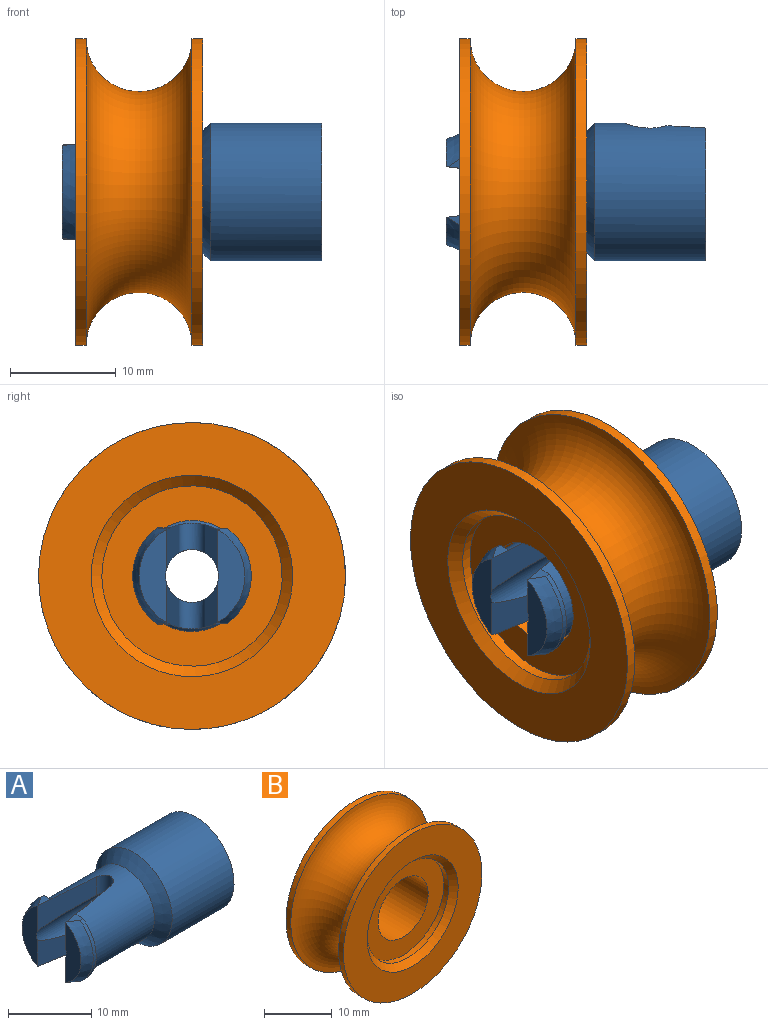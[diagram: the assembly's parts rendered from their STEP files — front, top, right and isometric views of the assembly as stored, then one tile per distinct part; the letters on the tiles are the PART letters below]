
ASSEMBLY  parts=2 mates=1
PART A: 35 faces, bbox 24.6x13.1x13.1 mm
  f0: cylinder r=5mm len=10.5mm, axis (-1,0,0), area 277.7mm2, adj f1,f2,f3,f12,f17,f21,f22,f23
  f1: plane 8.91x4.14mm, normal (-0.13,-0.99,0), area 27.1mm2, adj f0,f3,f5,f7,f15,f24,f32,f33
  f2: plane 8.91x4.14mm, normal (-0.13,0.99,0), area 27mm2, adj f0,f6,f7,f14,f24,f29,f30,f31
  f3: plane 9.12x3.46mm, normal (1,0,0), area 6.6mm2, adj f0,f1,f4,f23,f25,f34
  f4: cylinder r=5.6mm len=9.12mm, axis (-1,0,0), area 5.3mm2, adj f3,f5,f25,f34
  f5: cone r=5.6mm half-angle=21.8deg, axis (1,0,0), area 17.4mm2, adj f1,f4,f15,f23,f25,f34
  f6: plane 8.77x2.6mm, normal (-1,0,0), area 16.1mm2, adj f2,f7,f14,f22
  f7: cylinder r=2.5mm len=14.5mm, axis (-1,0,0), area 148.7mm2, adj f1,f2,f6,f15,f16,f21,f22,f23
  f8: cylinder r=4.5mm len=9mm, axis (-1,0,0), area 170mm2, adj f9,f16,f18,f19,f20
  f9: cone r=5.5mm half-angle=45deg, axis (1,0,0), area 37.6mm2, adj f8,f10,f18,f20
  f10: plane 13x12.54mm, normal (1,0,0), area 32.8mm2, adj f9,f11,f18,f20
  f11: cylinder r=6.5mm len=13mm, axis (-1,0,0), area 396.8mm2, adj f10,f17,f18,f19,f20
  f12: plane 9.04x3.46mm, normal (1,0,0), area 6.5mm2, adj f0,f13,f26,f31
  f13: cylinder r=5.6mm len=9.02mm, axis (-1,0,0), area 5.2mm2, adj f12,f14,f26,f31
  f14: cone r=5.6mm half-angle=21.8deg, axis (1,0,0), area 17.2mm2, adj f2,f6,f13,f22,f26,f31
  f15: plane 8.77x2.6mm, normal (-1,0,0), area 16.1mm2, adj f1,f5,f7,f23
  f16: cone r=4.5mm half-angle=45deg, axis (1,0,0), area 62.2mm2, adj f7,f8
  f17: cone r=5mm half-angle=45deg, axis (1,0,0), area 76.6mm2, adj f0,f11
  f18: plane 3.7x2.39mm, normal (0.17,0,-0.98), area 7.5mm2, adj f8,f9,f10,f11,f19
  f19: cylinder r=2.4mm len=4.8mm, axis (0,-1,0), area 23.8mm2, adj f8,f11,f18,f20
  f20: plane 3.7x2.39mm, normal (0.17,0,0.98), area 7.5mm2, adj f8,f9,f10,f11,f19
  f21: cylinder r=1.25mm len=2.83mm, axis (0,0,1), area 9.3mm2, adj f0,f7,f22,f23
  f22: plane 8.91x4.14mm, normal (-0.13,0.99,0), area 27mm2, adj f0,f6,f7,f14,f21,f26,f27,f28
  f23: plane 8.91x4.14mm, normal (-0.13,-0.99,0), area 27.1mm2, adj f0,f3,f5,f7,f15,f21,f25
  f24: cylinder r=1.25mm len=2.83mm, axis (0,0,1), area 9.3mm2, adj f0,f1,f2,f7
  f25: plane 1.92x1.21mm, normal (-0.05,-0.01,-1), area 1.3mm2, adj f3,f4,f5,f23
  f26: plane 2x1.29mm, normal (-0.05,-0.01,-1), area 1.4mm2, adj f12,f13,f14,f22
  f27: plane 0.06x0.02mm, normal (-1,0,0.05), area 0mm2, adj f0,f22,f28
  f28: plane 2.87x0.37mm, normal (-0.05,-0.01,-1), area 0.1mm2, adj f0,f22,f27
  f29: plane 3.74x0.49mm, normal (-0.05,-0.01,1), area 0.2mm2, adj f0,f2,f30
  f30: plane 0.07x0.02mm, normal (-1,0,-0.05), area 0mm2, adj f0,f2,f29
  f31: plane 2x1.29mm, normal (-0.05,-0.01,1), area 1.4mm2, adj f2,f12,f13,f14
  f32: plane 0.29x0.04mm, normal (-0.05,-0.01,1), area 0mm2, adj f0,f1,f33
  f33: plane 0x0mm, normal (-1,0,-0.05), area 0mm2, adj f0,f1,f32
  f34: plane 1.92x1.21mm, normal (-0.05,-0.01,1), area 1.3mm2, adj f1,f3,f4,f5
PART B: 12 faces, bbox 39.1x12x39.1 mm
  f0: cylinder r=14.5mm len=29mm, axis (0,1,0), area 91.1mm2, adj f1,f7
  f1: plane 29x29mm, normal (0,-1,0), area 375.9mm2, adj f0,f10
  f2: cylinder r=8.52mm len=17.04mm, axis (0,-1,0), area 53.5mm2, adj f3,f10
  f3: plane 17.04x17.04mm, normal (0,-1,0), area 141.4mm2, adj f2,f4
  f4: cylinder r=5.25mm len=10.5mm, axis (0,-1,0), area 263.9mm2, adj f3,f5
  f5: plane 17.04x17.04mm, normal (0,1,0), area 141.4mm2, adj f4,f6
  f6: cylinder r=8.52mm len=17.04mm, axis (0,-1,0), area 53.5mm2, adj f5,f11
  f7: torus R=14.5mm, axis (0,-1,0), area 1116.9mm2, adj f0,f9
  f8: plane 29x29mm, normal (0,1,0), area 375.9mm2, adj f9,f11
  f9: cylinder r=14.5mm len=29mm, axis (0,1,0), area 91.1mm2, adj f7,f8
  f10: cone r=9.52mm half-angle=45deg, axis (0,-1,0), area 80.1mm2, adj f1,f2
  f11: cone r=9.52mm half-angle=45deg, axis (0,1,0), area 80.1mm2, adj f6,f8
PLACE A t=(3.12,0.23,-2.35)mm fixed
PLACE B rot(axis=(0.7,0.7,-0.17),161.2deg) t=(-8.13,0.23,-2.35)mm
MATE revolute B.f2 <-> A.f0  axis (-1,0,0) through (-14.13,0.23,-2.35)mm
